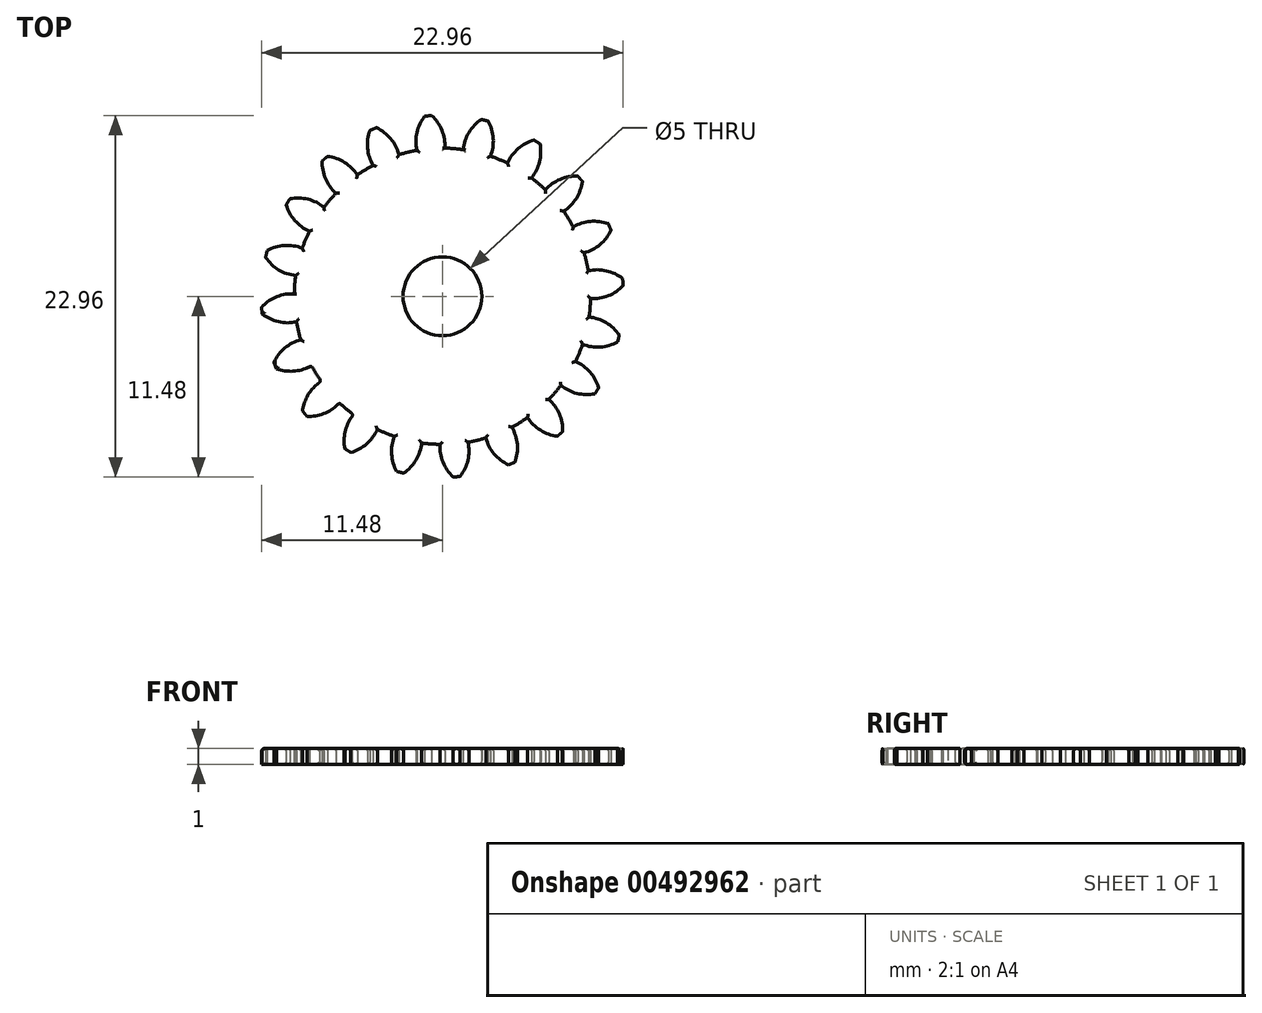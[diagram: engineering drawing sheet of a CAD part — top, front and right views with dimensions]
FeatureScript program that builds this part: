
annotation { "Feature Type Name" : "Feature", "Feature Type Description" : "" }
export const myFeature = defineFeature(function(context is Context, id is Id, definition is map)
    precondition{}
    {
        {
            assignVariable(context, id + "F0", {"name" : "GearDepth", "anyValue" : 1});
        }
        {
            var Q0;
            Q0=qCreatedBy(makeId("Top.planeOp"),FACE);
            var sketch = newSketch(context, id + "F1", { "sketchPlane" : qUnion([Q0])});
            skCircle(sketch, "E0", {"center": v(0, 0) * mm, "radius": 9.4 * mm});
            skCircle(sketch, "E1", {"center": v(0, 0) * mm, "radius": 10.45 * mm, "construction": true});
            skCircle(sketch, "E2", {"center": v(0, 0) * mm, "radius": 11.5 * mm, "construction": true});
            skLineSegment(sketch, "E3", {"start": v(0, 0) * mm, "end": v(0, 17.6) * mm, "construction": true});
            skLineSegment(sketch, "E4", {"start": v(0, 0) * mm, "end": v(-1.42, 18) * mm, "construction": true});
            skLineSegment(sketch, "E5", {"start": v(0, 10.45) * mm, "end": v(-10.54, 10.45) * mm, "construction": true});
            skLineSegment(sketch, "E6", {"start": v(0, 10.45) * mm, "end": v(-10.3, 6.7) * mm, "construction": true});
            skCircle(sketch, "E7", {"center": v(0, 10.45) * mm, "radius": 2.61 * mm, "construction": true});
            skCircle(sketch, "E8", {"center": v(-2.46, 9.56) * mm, "radius": 2.61 * mm, "construction": true});
            skArc(sketch, "E9", {"start": v(-4.91, 10.45) * mm, "mid": v(-4.92, 10.42) * mm, "end": v(-4.94, 10.39) * mm});
            skArc(sketch, "E10.trimOffspring", {"start": v(0.15, 9.4) * mm, "mid": v(-0.03, 10.54) * mm, "end": v(-0.68, 11.48) * mm});
            skArc(sketch, "E11.MirrorCS", {"start": v(-1.62, 9.27) * mm, "mid": v(-1.62, 10.41) * mm, "end": v(-1.12, 11.45) * mm});
            skLineSegment(sketch, "E12", {"start": v(-1.12, 11.45) * mm, "end": v(-0.68, 11.48) * mm});
            skArc(sketch, "E13.1.0", {"start": v(-2.76, 9) * mm, "mid": v(-3.29, 10.01) * mm, "end": v(-4.2, 10.7) * mm});
            skLineSegment(sketch, "E13.1.1", {"start": v(-4.6, 10.54) * mm, "end": v(-4.2, 10.7) * mm});
            skArc(sketch, "E13.1.2", {"start": v(-4.4, 8.31) * mm, "mid": v(-4.76, 9.4) * mm, "end": v(-4.6, 10.54) * mm});
            skArc(sketch, "E13.2.0", {"start": v(-5.4, 7.7) * mm, "mid": v(-6.22, 8.5) * mm, "end": v(-7.3, 8.89) * mm});
            skLineSegment(sketch, "E13.2.1", {"start": v(-7.64, 8.6) * mm, "end": v(-7.3, 8.89) * mm});
            skArc(sketch, "E13.2.2", {"start": v(-6.76, 6.54) * mm, "mid": v(-7.43, 7.47) * mm, "end": v(-7.64, 8.6) * mm});
            skArc(sketch, "E13.3.0", {"start": v(-7.52, 5.65) * mm, "mid": v(-8.54, 6.17) * mm, "end": v(-9.69, 6.2) * mm});
            skLineSegment(sketch, "E13.3.1", {"start": v(-9.92, 5.82) * mm, "end": v(-9.69, 6.2) * mm});
            skArc(sketch, "E13.3.2", {"start": v(-8.45, 4.13) * mm, "mid": v(-9.37, 4.81) * mm, "end": v(-9.92, 5.82) * mm});
            skArc(sketch, "E13.4.0", {"start": v(-8.9, 3.05) * mm, "mid": v(-10.03, 3.23) * mm, "end": v(-11.13, 2.9) * mm});
            skLineSegment(sketch, "E13.4.1", {"start": v(-11.23, 2.47) * mm, "end": v(-11.13, 2.9) * mm});
            skArc(sketch, "E13.4.2", {"start": v(-9.32, 1.32) * mm, "mid": v(-10.4, 1.68) * mm, "end": v(-11.23, 2.47) * mm});
            skArc(sketch, "E13.5.0", {"start": v(-9.4, 0.15) * mm, "mid": v(-10.54, -0.03) * mm, "end": v(-11.48, -0.68) * mm});
            skLineSegment(sketch, "E13.5.1", {"start": v(-11.45, -1.12) * mm, "end": v(-11.48, -0.68) * mm});
            skArc(sketch, "E13.5.2", {"start": v(-9.27, -1.62) * mm, "mid": v(-10.41, -1.62) * mm, "end": v(-11.45, -1.12) * mm});
            skArc(sketch, "E13.6.0", {"start": v(-9, -2.76) * mm, "mid": v(-10.01, -3.29) * mm, "end": v(-10.7, -4.2) * mm});
            skLineSegment(sketch, "E13.6.1", {"start": v(-10.54, -4.6) * mm, "end": v(-10.7, -4.2) * mm});
            skArc(sketch, "E13.6.2", {"start": v(-8.31, -4.4) * mm, "mid": v(-9.4, -4.76) * mm, "end": v(-10.54, -4.6) * mm});
            skArc(sketch, "E13.7.0", {"start": v(-7.7, -5.4) * mm, "mid": v(-8.5, -6.22) * mm, "end": v(-8.89, -7.3) * mm});
            skLineSegment(sketch, "E13.7.1", {"start": v(-8.6, -7.64) * mm, "end": v(-8.89, -7.3) * mm});
            skArc(sketch, "E13.7.2", {"start": v(-6.54, -6.76) * mm, "mid": v(-7.47, -7.43) * mm, "end": v(-8.6, -7.64) * mm});
            skArc(sketch, "E13.8.0", {"start": v(-5.65, -7.52) * mm, "mid": v(-6.17, -8.54) * mm, "end": v(-6.2, -9.69) * mm});
            skLineSegment(sketch, "E13.8.1", {"start": v(-5.82, -9.92) * mm, "end": v(-6.2, -9.69) * mm});
            skArc(sketch, "E13.8.2", {"start": v(-4.13, -8.45) * mm, "mid": v(-4.81, -9.37) * mm, "end": v(-5.82, -9.92) * mm});
            skArc(sketch, "E13.9.0", {"start": v(-3.05, -8.9) * mm, "mid": v(-3.23, -10.03) * mm, "end": v(-2.9, -11.13) * mm});
            skLineSegment(sketch, "E13.9.1", {"start": v(-2.47, -11.23) * mm, "end": v(-2.9, -11.13) * mm});
            skArc(sketch, "E13.9.2", {"start": v(-1.32, -9.32) * mm, "mid": v(-1.68, -10.4) * mm, "end": v(-2.47, -11.23) * mm});
            skArc(sketch, "E13.10.0", {"start": v(-0.15, -9.4) * mm, "mid": v(0.03, -10.54) * mm, "end": v(0.68, -11.48) * mm});
            skLineSegment(sketch, "E13.10.1", {"start": v(1.12, -11.45) * mm, "end": v(0.68, -11.48) * mm});
            skArc(sketch, "E13.10.2", {"start": v(1.62, -9.27) * mm, "mid": v(1.62, -10.41) * mm, "end": v(1.12, -11.45) * mm});
            skArc(sketch, "E13.11.0", {"start": v(2.76, -9) * mm, "mid": v(3.29, -10.01) * mm, "end": v(4.2, -10.7) * mm});
            skLineSegment(sketch, "E13.11.1", {"start": v(4.6, -10.54) * mm, "end": v(4.2, -10.7) * mm});
            skArc(sketch, "E13.11.2", {"start": v(4.4, -8.31) * mm, "mid": v(4.76, -9.4) * mm, "end": v(4.6, -10.54) * mm});
            skArc(sketch, "E13.12.0", {"start": v(5.4, -7.7) * mm, "mid": v(6.22, -8.5) * mm, "end": v(7.3, -8.89) * mm});
            skLineSegment(sketch, "E13.12.1", {"start": v(7.64, -8.6) * mm, "end": v(7.3, -8.89) * mm});
            skArc(sketch, "E13.12.2", {"start": v(6.76, -6.54) * mm, "mid": v(7.43, -7.47) * mm, "end": v(7.64, -8.6) * mm});
            skArc(sketch, "E13.13.0", {"start": v(7.52, -5.65) * mm, "mid": v(8.54, -6.17) * mm, "end": v(9.69, -6.2) * mm});
            skLineSegment(sketch, "E13.13.1", {"start": v(9.92, -5.82) * mm, "end": v(9.69, -6.2) * mm});
            skArc(sketch, "E13.13.2", {"start": v(8.45, -4.13) * mm, "mid": v(9.37, -4.81) * mm, "end": v(9.92, -5.82) * mm});
            skArc(sketch, "E13.14.0", {"start": v(8.9, -3.05) * mm, "mid": v(10.03, -3.23) * mm, "end": v(11.13, -2.9) * mm});
            skLineSegment(sketch, "E13.14.1", {"start": v(11.23, -2.47) * mm, "end": v(11.13, -2.9) * mm});
            skArc(sketch, "E13.14.2", {"start": v(9.32, -1.32) * mm, "mid": v(10.4, -1.68) * mm, "end": v(11.23, -2.47) * mm});
            skArc(sketch, "E13.15.0", {"start": v(9.4, -0.15) * mm, "mid": v(10.54, 0.03) * mm, "end": v(11.48, 0.68) * mm});
            skLineSegment(sketch, "E13.15.1", {"start": v(11.45, 1.12) * mm, "end": v(11.48, 0.68) * mm});
            skArc(sketch, "E13.15.2", {"start": v(9.27, 1.62) * mm, "mid": v(10.41, 1.62) * mm, "end": v(11.45, 1.12) * mm});
            skArc(sketch, "E13.16.0", {"start": v(9, 2.76) * mm, "mid": v(10.01, 3.29) * mm, "end": v(10.7, 4.2) * mm});
            skLineSegment(sketch, "E13.16.1", {"start": v(10.54, 4.6) * mm, "end": v(10.7, 4.2) * mm});
            skArc(sketch, "E13.16.2", {"start": v(8.31, 4.4) * mm, "mid": v(9.4, 4.76) * mm, "end": v(10.54, 4.6) * mm});
            skArc(sketch, "E13.17.0", {"start": v(7.7, 5.4) * mm, "mid": v(8.5, 6.22) * mm, "end": v(8.89, 7.3) * mm});
            skLineSegment(sketch, "E13.17.1", {"start": v(8.6, 7.64) * mm, "end": v(8.89, 7.3) * mm});
            skArc(sketch, "E13.17.2", {"start": v(6.54, 6.76) * mm, "mid": v(7.47, 7.43) * mm, "end": v(8.6, 7.64) * mm});
            skArc(sketch, "E13.18.0", {"start": v(5.65, 7.52) * mm, "mid": v(6.17, 8.54) * mm, "end": v(6.2, 9.69) * mm});
            skLineSegment(sketch, "E13.18.1", {"start": v(5.82, 9.92) * mm, "end": v(6.2, 9.69) * mm});
            skArc(sketch, "E13.18.2", {"start": v(4.13, 8.45) * mm, "mid": v(4.81, 9.37) * mm, "end": v(5.82, 9.92) * mm});
            skArc(sketch, "E13.19.0", {"start": v(3.05, 8.9) * mm, "mid": v(3.23, 10.03) * mm, "end": v(2.9, 11.13) * mm});
            skLineSegment(sketch, "E13.19.1", {"start": v(2.47, 11.23) * mm, "end": v(2.9, 11.13) * mm});
            skArc(sketch, "E13.19.2", {"start": v(1.32, 9.32) * mm, "mid": v(1.68, 10.4) * mm, "end": v(2.47, 11.23) * mm});
            skCircle(sketch, "E14", {"center": v(0, 0) * mm, "radius": 2.5 * mm});
            skSolve(sketch);
        }
        {
            var Q0;
            {var subQ0=sQuery(id+"F1.wireOp",EDGE,"E10.trimOffspring");Q0=makeQuery(id+"F1.imprint","IMPRINT",FACE,{"disambiguationData":[TD([[makeQuery(id+"F1.imprint","IMPRINT",EDGE,{"derivedFrom":subQ0}),1.0]])]});}
            var Q1;
            {var subQ0=sQuery(id+"F1.wireOp",EDGE,"E0");var subQ1=makeQuery(id+"F1.imprint","INTERSECT",VERTEX,{"derivedFrom":[subQ0,sQuery(id+"F1.wireOp",EDGE,"E10.trimOffspring")]});Q1=makeQuery(id+"F1.imprint","IMPRINT",FACE,{"disambiguationData":[TD([[makeQuery(id+"F1.imprint","IMPRINT",EDGE,{"disambiguationData":[TD([[subQ1,-1.0]])],"derivedFrom":subQ0}),1.0]])]});}
            var Q2;
            {var subQ0=sQuery(id+"F1.wireOp",EDGE,"E13.1.0");Q2=makeQuery(id+"F1.imprint","IMPRINT",FACE,{"disambiguationData":[TD([[makeQuery(id+"F1.imprint","IMPRINT",EDGE,{"derivedFrom":subQ0}),1.0]])]});}
            var Q3;
            {var subQ0=sQuery(id+"F1.wireOp",EDGE,"E13.2.0");Q3=makeQuery(id+"F1.imprint","IMPRINT",FACE,{"disambiguationData":[TD([[makeQuery(id+"F1.imprint","IMPRINT",EDGE,{"derivedFrom":subQ0}),1.0]])]});}
            var Q4;
            {var subQ0=sQuery(id+"F1.wireOp",EDGE,"E13.3.0");Q4=makeQuery(id+"F1.imprint","IMPRINT",FACE,{"disambiguationData":[TD([[makeQuery(id+"F1.imprint","IMPRINT",EDGE,{"derivedFrom":subQ0}),1.0]])]});}
            var Q5;
            {var subQ0=sQuery(id+"F1.wireOp",EDGE,"E13.4.0");Q5=makeQuery(id+"F1.imprint","IMPRINT",FACE,{"disambiguationData":[TD([[makeQuery(id+"F1.imprint","IMPRINT",EDGE,{"derivedFrom":subQ0}),1.0]])]});}
            var Q6;
            {var subQ0=sQuery(id+"F1.wireOp",EDGE,"E13.5.0");Q6=makeQuery(id+"F1.imprint","IMPRINT",FACE,{"disambiguationData":[TD([[makeQuery(id+"F1.imprint","IMPRINT",EDGE,{"derivedFrom":subQ0}),1.0]])]});}
            var Q7;
            {var subQ0=sQuery(id+"F1.wireOp",EDGE,"E13.6.0");Q7=makeQuery(id+"F1.imprint","IMPRINT",FACE,{"disambiguationData":[TD([[makeQuery(id+"F1.imprint","IMPRINT",EDGE,{"derivedFrom":subQ0}),1.0]])]});}
            var Q8;
            {var subQ0=sQuery(id+"F1.wireOp",EDGE,"E13.7.0");Q8=makeQuery(id+"F1.imprint","IMPRINT",FACE,{"disambiguationData":[TD([[makeQuery(id+"F1.imprint","IMPRINT",EDGE,{"derivedFrom":subQ0}),1.0]])]});}
            var Q9;
            {var subQ0=sQuery(id+"F1.wireOp",EDGE,"E13.8.0");Q9=makeQuery(id+"F1.imprint","IMPRINT",FACE,{"disambiguationData":[TD([[makeQuery(id+"F1.imprint","IMPRINT",EDGE,{"derivedFrom":subQ0}),1.0]])]});}
            var Q10;
            {var subQ0=sQuery(id+"F1.wireOp",EDGE,"E13.9.0");Q10=makeQuery(id+"F1.imprint","IMPRINT",FACE,{"disambiguationData":[TD([[makeQuery(id+"F1.imprint","IMPRINT",EDGE,{"derivedFrom":subQ0}),1.0]])]});}
            var Q11;
            {var subQ0=sQuery(id+"F1.wireOp",EDGE,"E13.10.0");Q11=makeQuery(id+"F1.imprint","IMPRINT",FACE,{"disambiguationData":[TD([[makeQuery(id+"F1.imprint","IMPRINT",EDGE,{"derivedFrom":subQ0}),1.0]])]});}
            var Q12;
            {var subQ0=sQuery(id+"F1.wireOp",EDGE,"E13.11.0");Q12=makeQuery(id+"F1.imprint","IMPRINT",FACE,{"disambiguationData":[TD([[makeQuery(id+"F1.imprint","IMPRINT",EDGE,{"derivedFrom":subQ0}),1.0]])]});}
            var Q13;
            {var subQ0=sQuery(id+"F1.wireOp",EDGE,"E13.12.0");Q13=makeQuery(id+"F1.imprint","IMPRINT",FACE,{"disambiguationData":[TD([[makeQuery(id+"F1.imprint","IMPRINT",EDGE,{"derivedFrom":subQ0}),1.0]])]});}
            var Q14;
            {var subQ0=sQuery(id+"F1.wireOp",EDGE,"E13.13.0");Q14=makeQuery(id+"F1.imprint","IMPRINT",FACE,{"disambiguationData":[TD([[makeQuery(id+"F1.imprint","IMPRINT",EDGE,{"derivedFrom":subQ0}),1.0]])]});}
            var Q15;
            {var subQ0=sQuery(id+"F1.wireOp",EDGE,"E13.14.0");Q15=makeQuery(id+"F1.imprint","IMPRINT",FACE,{"disambiguationData":[TD([[makeQuery(id+"F1.imprint","IMPRINT",EDGE,{"derivedFrom":subQ0}),1.0]])]});}
            var Q16;
            {var subQ0=sQuery(id+"F1.wireOp",EDGE,"E13.15.0");Q16=makeQuery(id+"F1.imprint","IMPRINT",FACE,{"disambiguationData":[TD([[makeQuery(id+"F1.imprint","IMPRINT",EDGE,{"derivedFrom":subQ0}),1.0]])]});}
            var Q17;
            {var subQ0=sQuery(id+"F1.wireOp",EDGE,"E13.16.0");Q17=makeQuery(id+"F1.imprint","IMPRINT",FACE,{"disambiguationData":[TD([[makeQuery(id+"F1.imprint","IMPRINT",EDGE,{"derivedFrom":subQ0}),1.0]])]});}
            var Q18;
            {var subQ0=sQuery(id+"F1.wireOp",EDGE,"E13.17.0");Q18=makeQuery(id+"F1.imprint","IMPRINT",FACE,{"disambiguationData":[TD([[makeQuery(id+"F1.imprint","IMPRINT",EDGE,{"derivedFrom":subQ0}),1.0]])]});}
            var Q19;
            {var subQ0=sQuery(id+"F1.wireOp",EDGE,"E13.18.0");Q19=makeQuery(id+"F1.imprint","IMPRINT",FACE,{"disambiguationData":[TD([[makeQuery(id+"F1.imprint","IMPRINT",EDGE,{"derivedFrom":subQ0}),1.0]])]});}
            var Q20;
            {var subQ0=sQuery(id+"F1.wireOp",EDGE,"E13.19.0");Q20=makeQuery(id+"F1.imprint","IMPRINT",FACE,{"disambiguationData":[TD([[makeQuery(id+"F1.imprint","IMPRINT",EDGE,{"derivedFrom":subQ0}),1.0]])]});}
            var Q21;
            Q21=sQuery(id+"F1.wireOp",EDGE,"E0");
            var Q22;
            Q22=sQuery(id+"F1.wireOp",EDGE,"E10.trimOffspring");
            var Q23;
            Q23=sQuery(id+"F1.wireOp",EDGE,"E12");
            var Q24;
            Q24=sQuery(id+"F1.wireOp",EDGE,"E11.MirrorCS");
            extrude(context, id + "F2", {"entities" : qUnion([Q0, Q1, Q2, Q3, Q4, Q5, Q6, Q7, Q8, Q9, Q10, Q11, Q12, Q13, Q14, Q15, Q16, Q17, Q18, Q19, Q20]), "surfaceEntities" : qUnion([Q21, Q22, Q23, Q24]), "depth" : (getVariable(context, 'GearDepth')) * mm});
        }
        {
            var Q0;
            Q0=makeQuery(id+"F2.opExtrude","CAP_EDGE",EDGE,{"disambiguationData":[OSD([sQuery(id+"F1.wireOp",EDGE,"E13.5.2")])],"isStart":false});
            var Q1;
            Q1=makeQuery(id+"F2.opExtrude","CAP_EDGE",EDGE,{"disambiguationData":[OSD([sQuery(id+"F1.wireOp",EDGE,"E13.5.1")])],"isStart":false});
            var Q2;
            {var subQ0=sQuery(id+"F1.wireOp",EDGE,"E0");Q2=makeQuery(id+"F2.opExtrude","CAP_EDGE",EDGE,{"disambiguationData":[OSD([subQ0]),TDD([makeQuery(id+"F1.imprint","IMPRINT",EDGE,{"disambiguationData":[TD([[makeQuery(id+"F1.imprint","INTERSECT",VERTEX,{"derivedFrom":[subQ0,sQuery(id+"F1.wireOp",EDGE,"E13.5.2")]}),-1.0]])],"derivedFrom":subQ0})])],"isStart":false});}
            var Q3;
            Q3=makeQuery(id+"F2.opExtrude","CAP_EDGE",EDGE,{"disambiguationData":[OSD([sQuery(id+"F1.wireOp",EDGE,"E13.6.0")])],"isStart":false});
            var Q4;
            Q4=makeQuery(id+"F2.opExtrude","CAP_EDGE",EDGE,{"disambiguationData":[OSD([sQuery(id+"F1.wireOp",EDGE,"E13.6.1")])],"isStart":false});
            var Q5;
            Q5=makeQuery(id+"F2.opExtrude","CAP_EDGE",EDGE,{"disambiguationData":[OSD([sQuery(id+"F1.wireOp",EDGE,"E13.6.2")])],"isStart":false});
            var Q6;
            {var subQ0=sQuery(id+"F1.wireOp",EDGE,"E0");Q6=makeQuery(id+"F2.opExtrude","SWEPT_FACE",FACE,{"disambiguationData":[OSD([subQ0]),TDD([makeQuery(id+"F1.imprint","IMPRINT",EDGE,{"disambiguationData":[TD([[makeQuery(id+"F1.imprint","INTERSECT",VERTEX,{"derivedFrom":[subQ0,sQuery(id+"F1.wireOp",EDGE,"E13.6.2")]}),-1.0]])],"derivedFrom":subQ0})])]});}
            var Q7;
            {var subQ0=sQuery(id+"F1.wireOp",EDGE,"E0");Q7=makeQuery(id+"F2.opExtrude","CAP_EDGE",EDGE,{"disambiguationData":[OSD([subQ0]),TDD([makeQuery(id+"F1.imprint","IMPRINT",EDGE,{"disambiguationData":[TD([[makeQuery(id+"F1.imprint","INTERSECT",VERTEX,{"derivedFrom":[subQ0,sQuery(id+"F1.wireOp",EDGE,"E13.6.2")]}),-1.0]])],"derivedFrom":subQ0})])],"isStart":false});}
            var Q8;
            Q8=makeQuery(id+"F2.opExtrude","CAP_EDGE",EDGE,{"disambiguationData":[OSD([sQuery(id+"F1.wireOp",EDGE,"E13.7.2")])],"isStart":true});
            var Q9;
            {var subQ0=sQuery(id+"F1.wireOp",EDGE,"E0");Q9=makeQuery(id+"F2.opExtrude","CAP_EDGE",EDGE,{"disambiguationData":[OSD([subQ0]),TDD([makeQuery(id+"F1.imprint","IMPRINT",EDGE,{"disambiguationData":[TD([[makeQuery(id+"F1.imprint","INTERSECT",VERTEX,{"derivedFrom":[subQ0,sQuery(id+"F1.wireOp",EDGE,"E13.7.2")]}),-1.0]])],"derivedFrom":subQ0})])],"isStart":true});}
            var Q10;
            Q10=makeQuery(id+"F2.opExtrude","CAP_EDGE",EDGE,{"disambiguationData":[OSD([sQuery(id+"F1.wireOp",EDGE,"E13.7.2")])],"isStart":false});
            var Q11;
            {var subQ0=sQuery(id+"F1.wireOp",EDGE,"E0");Q11=makeQuery(id+"F2.opExtrude","CAP_EDGE",EDGE,{"disambiguationData":[OSD([subQ0]),TDD([makeQuery(id+"F1.imprint","IMPRINT",EDGE,{"disambiguationData":[TD([[makeQuery(id+"F1.imprint","INTERSECT",VERTEX,{"derivedFrom":[subQ0,sQuery(id+"F1.wireOp",EDGE,"E13.7.2")]}),-1.0]])],"derivedFrom":subQ0})])],"isStart":false});}
            var Q12;
            Q12=makeQuery(id+"F2.opExtrude","CAP_EDGE",EDGE,{"disambiguationData":[OSD([sQuery(id+"F1.wireOp",EDGE,"E13.8.0")])],"isStart":false});
            var Q13;
            {var subQ0=sQuery(id+"F1.wireOp",EDGE,"E0");Q13=makeQuery(id+"F2.opExtrude","SWEPT_FACE",FACE,{"disambiguationData":[OSD([subQ0]),TDD([makeQuery(id+"F1.imprint","IMPRINT",EDGE,{"disambiguationData":[TD([[makeQuery(id+"F1.imprint","INTERSECT",VERTEX,{"derivedFrom":[subQ0,sQuery(id+"F1.wireOp",EDGE,"E13.7.2")]}),-1.0]])],"derivedFrom":subQ0})])]});}
            var Q14;
            Q14=makeQuery(id+"F2.opExtrude","CAP_EDGE",EDGE,{"disambiguationData":[OSD([sQuery(id+"F1.wireOp",EDGE,"E13.6.0")])],"isStart":true});
            var Q15;
            Q15=makeQuery(id+"F2.opExtrude","CAP_EDGE",EDGE,{"disambiguationData":[OSD([sQuery(id+"F1.wireOp",EDGE,"E13.8.2")])],"isStart":false});
            var Q16;
            {var subQ0=sQuery(id+"F1.wireOp",EDGE,"E0");Q16=makeQuery(id+"F2.opExtrude","CAP_EDGE",EDGE,{"disambiguationData":[OSD([subQ0]),TDD([makeQuery(id+"F1.imprint","IMPRINT",EDGE,{"disambiguationData":[TD([[makeQuery(id+"F1.imprint","INTERSECT",VERTEX,{"derivedFrom":[subQ0,sQuery(id+"F1.wireOp",EDGE,"E13.8.2")]}),-1.0]])],"derivedFrom":subQ0})])],"isStart":false});}
            var Q17;
            Q17=makeQuery(id+"F2.opExtrude","CAP_EDGE",EDGE,{"disambiguationData":[OSD([sQuery(id+"F1.wireOp",EDGE,"E13.9.0")])],"isStart":false});
            var Q18;
            Q18=makeQuery(id+"F2.opExtrude","CAP_EDGE",EDGE,{"disambiguationData":[OSD([sQuery(id+"F1.wireOp",EDGE,"E13.9.2")])],"isStart":false});
            var Q19;
            {var subQ0=sQuery(id+"F1.wireOp",EDGE,"E0");Q19=makeQuery(id+"F2.opExtrude","CAP_EDGE",EDGE,{"disambiguationData":[OSD([subQ0]),TDD([makeQuery(id+"F1.imprint","IMPRINT",EDGE,{"disambiguationData":[TD([[makeQuery(id+"F1.imprint","INTERSECT",VERTEX,{"derivedFrom":[subQ0,sQuery(id+"F1.wireOp",EDGE,"E13.9.2")]}),-1.0]])],"derivedFrom":subQ0})])],"isStart":false});}
            var Q20;
            Q20=makeQuery(id+"F2.opExtrude","CAP_EDGE",EDGE,{"disambiguationData":[OSD([sQuery(id+"F1.wireOp",EDGE,"E13.10.0")])],"isStart":false});
            var Q21;
            Q21=makeQuery(id+"F2.opExtrude","CAP_EDGE",EDGE,{"disambiguationData":[OSD([sQuery(id+"F1.wireOp",EDGE,"E13.10.2")])],"isStart":false});
            var Q22;
            {var subQ0=sQuery(id+"F1.wireOp",EDGE,"E0");Q22=makeQuery(id+"F2.opExtrude","CAP_EDGE",EDGE,{"disambiguationData":[OSD([subQ0]),TDD([makeQuery(id+"F1.imprint","IMPRINT",EDGE,{"disambiguationData":[TD([[makeQuery(id+"F1.imprint","INTERSECT",VERTEX,{"derivedFrom":[subQ0,sQuery(id+"F1.wireOp",EDGE,"E13.10.2")]}),-1.0]])],"derivedFrom":subQ0})])],"isStart":false});}
            var Q23;
            Q23=makeQuery(id+"F2.opExtrude","CAP_EDGE",EDGE,{"disambiguationData":[OSD([sQuery(id+"F1.wireOp",EDGE,"E13.11.0")])],"isStart":false});
            var Q24;
            Q24=makeQuery(id+"F2.opExtrude","CAP_EDGE",EDGE,{"disambiguationData":[OSD([sQuery(id+"F1.wireOp",EDGE,"E13.11.2")])],"isStart":false});
            var Q25;
            {var subQ0=sQuery(id+"F1.wireOp",EDGE,"E0");Q25=makeQuery(id+"F2.opExtrude","CAP_EDGE",EDGE,{"disambiguationData":[OSD([subQ0]),TDD([makeQuery(id+"F1.imprint","IMPRINT",EDGE,{"disambiguationData":[TD([[makeQuery(id+"F1.imprint","INTERSECT",VERTEX,{"derivedFrom":[subQ0,sQuery(id+"F1.wireOp",EDGE,"E13.11.2")]}),-1.0]])],"derivedFrom":subQ0})])],"isStart":false});}
            var Q26;
            Q26=makeQuery(id+"F2.opExtrude","CAP_EDGE",EDGE,{"disambiguationData":[OSD([sQuery(id+"F1.wireOp",EDGE,"E13.12.0")])],"isStart":false});
            var Q27;
            Q27=makeQuery(id+"F2.opExtrude","CAP_EDGE",EDGE,{"disambiguationData":[OSD([sQuery(id+"F1.wireOp",EDGE,"E13.12.2")])],"isStart":false});
            var Q28;
            {var subQ0=sQuery(id+"F1.wireOp",EDGE,"E0");Q28=makeQuery(id+"F2.opExtrude","CAP_EDGE",EDGE,{"disambiguationData":[OSD([subQ0]),TDD([makeQuery(id+"F1.imprint","IMPRINT",EDGE,{"disambiguationData":[TD([[makeQuery(id+"F1.imprint","INTERSECT",VERTEX,{"derivedFrom":[subQ0,sQuery(id+"F1.wireOp",EDGE,"E13.12.2")]}),-1.0]])],"derivedFrom":subQ0})])],"isStart":false});}
            var Q29;
            Q29=makeQuery(id+"F2.opExtrude","CAP_EDGE",EDGE,{"disambiguationData":[OSD([sQuery(id+"F1.wireOp",EDGE,"E13.13.0")])],"isStart":false});
            var Q30;
            Q30=makeQuery(id+"F2.opExtrude","CAP_EDGE",EDGE,{"disambiguationData":[OSD([sQuery(id+"F1.wireOp",EDGE,"E13.13.2")])],"isStart":false});
            var Q31;
            {var subQ0=sQuery(id+"F1.wireOp",EDGE,"E0");Q31=makeQuery(id+"F2.opExtrude","CAP_EDGE",EDGE,{"disambiguationData":[OSD([subQ0]),TDD([makeQuery(id+"F1.imprint","IMPRINT",EDGE,{"disambiguationData":[TD([[makeQuery(id+"F1.imprint","INTERSECT",VERTEX,{"derivedFrom":[subQ0,sQuery(id+"F1.wireOp",EDGE,"E13.13.2")]}),-1.0]])],"derivedFrom":subQ0})])],"isStart":false});}
            var Q32;
            Q32=makeQuery(id+"F2.opExtrude","CAP_EDGE",EDGE,{"disambiguationData":[OSD([sQuery(id+"F1.wireOp",EDGE,"E13.14.0")])],"isStart":false});
            var Q33;
            Q33=makeQuery(id+"F2.opExtrude","CAP_EDGE",EDGE,{"disambiguationData":[OSD([sQuery(id+"F1.wireOp",EDGE,"E13.14.2")])],"isStart":false});
            var Q34;
            {var subQ0=sQuery(id+"F1.wireOp",EDGE,"E0");Q34=makeQuery(id+"F2.opExtrude","CAP_EDGE",EDGE,{"disambiguationData":[OSD([subQ0]),TDD([makeQuery(id+"F1.imprint","IMPRINT",EDGE,{"disambiguationData":[TD([[makeQuery(id+"F1.imprint","INTERSECT",VERTEX,{"derivedFrom":[subQ0,sQuery(id+"F1.wireOp",EDGE,"E13.14.2")]}),-1.0]])],"derivedFrom":subQ0})])],"isStart":false});}
            var Q35;
            Q35=makeQuery(id+"F2.opExtrude","CAP_EDGE",EDGE,{"disambiguationData":[OSD([sQuery(id+"F1.wireOp",EDGE,"E13.15.0")])],"isStart":false});
            var Q36;
            {var subQ0=sQuery(id+"F1.wireOp",EDGE,"E0");Q36=makeQuery(id+"F2.opExtrude","CAP_EDGE",EDGE,{"disambiguationData":[OSD([subQ0]),TDD([makeQuery(id+"F1.imprint","IMPRINT",EDGE,{"disambiguationData":[TD([[makeQuery(id+"F1.imprint","INTERSECT",VERTEX,{"derivedFrom":[subQ0,sQuery(id+"F1.wireOp",EDGE,"E13.14.2")]}),-1.0]])],"derivedFrom":subQ0})])],"isStart":false});}
            var Q37;
            Q37=makeQuery(id+"F2.opExtrude","CAP_EDGE",EDGE,{"disambiguationData":[OSD([sQuery(id+"F1.wireOp",EDGE,"E13.15.2")])],"isStart":false});
            var Q38;
            {var subQ0=sQuery(id+"F1.wireOp",EDGE,"E0");Q38=makeQuery(id+"F2.opExtrude","CAP_EDGE",EDGE,{"disambiguationData":[OSD([subQ0]),TDD([makeQuery(id+"F1.imprint","IMPRINT",EDGE,{"disambiguationData":[TD([[makeQuery(id+"F1.imprint","INTERSECT",VERTEX,{"derivedFrom":[subQ0,sQuery(id+"F1.wireOp",EDGE,"E13.15.2")]}),-1.0]])],"derivedFrom":subQ0})])],"isStart":false});}
            var Q39;
            Q39=makeQuery(id+"F2.opExtrude","CAP_EDGE",EDGE,{"disambiguationData":[OSD([sQuery(id+"F1.wireOp",EDGE,"E13.16.0")])],"isStart":false});
            var Q40;
            Q40=makeQuery(id+"F2.opExtrude","CAP_EDGE",EDGE,{"disambiguationData":[OSD([sQuery(id+"F1.wireOp",EDGE,"E13.16.2")])],"isStart":false});
            var Q41;
            Q41=makeQuery(id+"F2.opExtrude","CAP_EDGE",EDGE,{"disambiguationData":[OSD([sQuery(id+"F1.wireOp",EDGE,"E13.17.0")])],"isStart":false});
            var Q42;
            {var subQ0=sQuery(id+"F1.wireOp",EDGE,"E0");Q42=makeQuery(id+"F2.opExtrude","CAP_EDGE",EDGE,{"disambiguationData":[OSD([subQ0]),TDD([makeQuery(id+"F1.imprint","IMPRINT",EDGE,{"disambiguationData":[TD([[makeQuery(id+"F1.imprint","INTERSECT",VERTEX,{"derivedFrom":[subQ0,sQuery(id+"F1.wireOp",EDGE,"E13.16.2")]}),-1.0]])],"derivedFrom":subQ0})])],"isStart":false});}
            var Q43;
            Q43=makeQuery(id+"F2.opExtrude","CAP_EDGE",EDGE,{"disambiguationData":[OSD([sQuery(id+"F1.wireOp",EDGE,"E13.17.2")])],"isStart":false});
            var Q44;
            {var subQ0=sQuery(id+"F1.wireOp",EDGE,"E0");Q44=makeQuery(id+"F2.opExtrude","CAP_EDGE",EDGE,{"disambiguationData":[OSD([subQ0]),TDD([makeQuery(id+"F1.imprint","IMPRINT",EDGE,{"disambiguationData":[TD([[makeQuery(id+"F1.imprint","INTERSECT",VERTEX,{"derivedFrom":[subQ0,sQuery(id+"F1.wireOp",EDGE,"E13.17.2")]}),-1.0]])],"derivedFrom":subQ0})])],"isStart":false});}
            var Q45;
            Q45=makeQuery(id+"F2.opExtrude","CAP_EDGE",EDGE,{"disambiguationData":[OSD([sQuery(id+"F1.wireOp",EDGE,"E13.18.0")])],"isStart":false});
            var Q46;
            Q46=makeQuery(id+"F2.opExtrude","CAP_EDGE",EDGE,{"disambiguationData":[OSD([sQuery(id+"F1.wireOp",EDGE,"E13.18.2")])],"isStart":false});
            var Q47;
            {var subQ0=sQuery(id+"F1.wireOp",EDGE,"E0");Q47=makeQuery(id+"F2.opExtrude","CAP_EDGE",EDGE,{"disambiguationData":[OSD([subQ0]),TDD([makeQuery(id+"F1.imprint","IMPRINT",EDGE,{"disambiguationData":[TD([[makeQuery(id+"F1.imprint","INTERSECT",VERTEX,{"derivedFrom":[subQ0,sQuery(id+"F1.wireOp",EDGE,"E13.18.2")]}),-1.0]])],"derivedFrom":subQ0})])],"isStart":false});}
            var Q48;
            Q48=makeQuery(id+"F2.opExtrude","CAP_EDGE",EDGE,{"disambiguationData":[OSD([sQuery(id+"F1.wireOp",EDGE,"E13.19.0")])],"isStart":false});
            var Q49;
            Q49=makeQuery(id+"F2.opExtrude","CAP_EDGE",EDGE,{"disambiguationData":[OSD([sQuery(id+"F1.wireOp",EDGE,"E13.19.2")])],"isStart":false});
            var Q50;
            Q50=makeQuery(id+"F2.opExtrude","CAP_EDGE",EDGE,{"disambiguationData":[OSD([sQuery(id+"F1.wireOp",EDGE,"E10.trimOffspring")])],"isStart":false});
            var Q51;
            Q51=makeQuery(id+"F2.opExtrude","CAP_EDGE",EDGE,{"disambiguationData":[OSD([sQuery(id+"F1.wireOp",EDGE,"E11.MirrorCS")])],"isStart":false});
            var Q52;
            {var subQ0=sQuery(id+"F1.wireOp",EDGE,"E0");Q52=makeQuery(id+"F2.opExtrude","CAP_EDGE",EDGE,{"disambiguationData":[OSD([subQ0]),TDD([makeQuery(id+"F1.imprint","IMPRINT",EDGE,{"disambiguationData":[TD([[makeQuery(id+"F1.imprint","INTERSECT",VERTEX,{"derivedFrom":[subQ0,sQuery(id+"F1.wireOp",EDGE,"E11.MirrorCS")]}),-1.0]])],"derivedFrom":subQ0})])],"isStart":false});}
            var Q53;
            Q53=makeQuery(id+"F2.opExtrude","CAP_EDGE",EDGE,{"disambiguationData":[OSD([sQuery(id+"F1.wireOp",EDGE,"E13.1.0")])],"isStart":false});
            var Q54;
            Q54=makeQuery(id+"F2.opExtrude","CAP_EDGE",EDGE,{"disambiguationData":[OSD([sQuery(id+"F1.wireOp",EDGE,"E13.1.2")])],"isStart":false});
            var Q55;
            {var subQ0=sQuery(id+"F1.wireOp",EDGE,"E0");Q55=makeQuery(id+"F2.opExtrude","CAP_EDGE",EDGE,{"disambiguationData":[OSD([subQ0]),TDD([makeQuery(id+"F1.imprint","IMPRINT",EDGE,{"disambiguationData":[TD([[makeQuery(id+"F1.imprint","INTERSECT",VERTEX,{"derivedFrom":[subQ0,sQuery(id+"F1.wireOp",EDGE,"E13.1.2")]}),-1.0]])],"derivedFrom":subQ0})])],"isStart":false});}
            var Q56;
            Q56=makeQuery(id+"F2.opExtrude","CAP_EDGE",EDGE,{"disambiguationData":[OSD([sQuery(id+"F1.wireOp",EDGE,"E13.2.0")])],"isStart":false});
            var Q57;
            Q57=makeQuery(id+"F2.opExtrude","CAP_EDGE",EDGE,{"disambiguationData":[OSD([sQuery(id+"F1.wireOp",EDGE,"E13.2.2")])],"isStart":false});
            var Q58;
            {var subQ0=sQuery(id+"F1.wireOp",EDGE,"E0");Q58=makeQuery(id+"F2.opExtrude","CAP_EDGE",EDGE,{"disambiguationData":[OSD([subQ0]),TDD([makeQuery(id+"F1.imprint","IMPRINT",EDGE,{"disambiguationData":[TD([[makeQuery(id+"F1.imprint","INTERSECT",VERTEX,{"derivedFrom":[subQ0,sQuery(id+"F1.wireOp",EDGE,"E13.2.2")]}),-1.0]])],"derivedFrom":subQ0})])],"isStart":false});}
            var Q59;
            Q59=makeQuery(id+"F2.opExtrude","CAP_EDGE",EDGE,{"disambiguationData":[OSD([sQuery(id+"F1.wireOp",EDGE,"E13.3.0")])],"isStart":false});
            var Q60;
            Q60=makeQuery(id+"F2.opExtrude","CAP_EDGE",EDGE,{"disambiguationData":[OSD([sQuery(id+"F1.wireOp",EDGE,"E13.3.2")])],"isStart":false});
            var Q61;
            {var subQ0=sQuery(id+"F1.wireOp",EDGE,"E0");Q61=makeQuery(id+"F2.opExtrude","CAP_EDGE",EDGE,{"disambiguationData":[OSD([subQ0]),TDD([makeQuery(id+"F1.imprint","IMPRINT",EDGE,{"disambiguationData":[TD([[makeQuery(id+"F1.imprint","INTERSECT",VERTEX,{"derivedFrom":[subQ0,sQuery(id+"F1.wireOp",EDGE,"E13.3.2")]}),-1.0]])],"derivedFrom":subQ0})])],"isStart":false});}
            var Q62;
            Q62=makeQuery(id+"F2.opExtrude","CAP_EDGE",EDGE,{"disambiguationData":[OSD([sQuery(id+"F1.wireOp",EDGE,"E13.4.0")])],"isStart":false});
            var Q63;
            Q63=makeQuery(id+"F2.opExtrude","CAP_EDGE",EDGE,{"disambiguationData":[OSD([sQuery(id+"F1.wireOp",EDGE,"E13.4.2")])],"isStart":false});
            var Q64;
            {var subQ0=sQuery(id+"F1.wireOp",EDGE,"E0");Q64=makeQuery(id+"F2.opExtrude","CAP_EDGE",EDGE,{"disambiguationData":[OSD([subQ0]),TDD([makeQuery(id+"F1.imprint","IMPRINT",EDGE,{"disambiguationData":[TD([[makeQuery(id+"F1.imprint","INTERSECT",VERTEX,{"derivedFrom":[subQ0,sQuery(id+"F1.wireOp",EDGE,"E13.4.2")]}),-1.0]])],"derivedFrom":subQ0})])],"isStart":false});}
            var Q65;
            {var subQ0=sQuery(id+"F1.wireOp",EDGE,"E0");Q65=makeQuery(id+"F2.opExtrude","CAP_EDGE",EDGE,{"disambiguationData":[OSD([subQ0]),TDD([makeQuery(id+"F1.imprint","IMPRINT",EDGE,{"disambiguationData":[TD([[makeQuery(id+"F1.imprint","INTERSECT",VERTEX,{"derivedFrom":[subQ0,sQuery(id+"F1.wireOp",EDGE,"E13.5.2")]}),-1.0]])],"derivedFrom":subQ0})])],"isStart":true});}
            var Q66;
            Q66=makeQuery(id+"F2.opExtrude","CAP_EDGE",EDGE,{"disambiguationData":[OSD([sQuery(id+"F1.wireOp",EDGE,"E13.5.2")])],"isStart":true});
            var Q67;
            {var subQ0=sQuery(id+"F1.wireOp",EDGE,"E0");Q67=makeQuery(id+"F2.opExtrude","CAP_EDGE",EDGE,{"disambiguationData":[OSD([subQ0]),TDD([makeQuery(id+"F1.imprint","IMPRINT",EDGE,{"disambiguationData":[TD([[makeQuery(id+"F1.imprint","INTERSECT",VERTEX,{"derivedFrom":[subQ0,sQuery(id+"F1.wireOp",EDGE,"E13.4.2")]}),-1.0]])],"derivedFrom":subQ0})])],"isStart":true});}
            var Q68;
            Q68=makeQuery(id+"F2.opExtrude","CAP_EDGE",EDGE,{"disambiguationData":[OSD([sQuery(id+"F1.wireOp",EDGE,"E13.4.2")])],"isStart":true});
            var Q69;
            Q69=makeQuery(id+"F2.opExtrude","CAP_EDGE",EDGE,{"disambiguationData":[OSD([sQuery(id+"F1.wireOp",EDGE,"E13.4.0")])],"isStart":true});
            var Q70;
            {var subQ0=sQuery(id+"F1.wireOp",EDGE,"E0");Q70=makeQuery(id+"F2.opExtrude","CAP_EDGE",EDGE,{"disambiguationData":[OSD([subQ0]),TDD([makeQuery(id+"F1.imprint","IMPRINT",EDGE,{"disambiguationData":[TD([[makeQuery(id+"F1.imprint","INTERSECT",VERTEX,{"derivedFrom":[subQ0,sQuery(id+"F1.wireOp",EDGE,"E13.3.2")]}),-1.0]])],"derivedFrom":subQ0})])],"isStart":true});}
            var Q71;
            Q71=makeQuery(id+"F2.opExtrude","CAP_EDGE",EDGE,{"disambiguationData":[OSD([sQuery(id+"F1.wireOp",EDGE,"E13.3.2")])],"isStart":true});
            var Q72;
            Q72=makeQuery(id+"F2.opExtrude","CAP_EDGE",EDGE,{"disambiguationData":[OSD([sQuery(id+"F1.wireOp",EDGE,"E13.3.0")])],"isStart":true});
            var Q73;
            {var subQ0=sQuery(id+"F1.wireOp",EDGE,"E0");Q73=makeQuery(id+"F2.opExtrude","CAP_EDGE",EDGE,{"disambiguationData":[OSD([subQ0]),TDD([makeQuery(id+"F1.imprint","IMPRINT",EDGE,{"disambiguationData":[TD([[makeQuery(id+"F1.imprint","INTERSECT",VERTEX,{"derivedFrom":[subQ0,sQuery(id+"F1.wireOp",EDGE,"E13.2.2")]}),-1.0]])],"derivedFrom":subQ0})])],"isStart":true});}
            var Q74;
            Q74=makeQuery(id+"F2.opExtrude","CAP_EDGE",EDGE,{"disambiguationData":[OSD([sQuery(id+"F1.wireOp",EDGE,"E13.2.2")])],"isStart":true});
            var Q75;
            Q75=makeQuery(id+"F2.opExtrude","CAP_EDGE",EDGE,{"disambiguationData":[OSD([sQuery(id+"F1.wireOp",EDGE,"E13.2.0")])],"isStart":true});
            var Q76;
            Q76=makeQuery(id+"F2.opExtrude","CAP_EDGE",EDGE,{"disambiguationData":[OSD([sQuery(id+"F1.wireOp",EDGE,"E13.1.2")])],"isStart":true});
            var Q77;
            {var subQ0=sQuery(id+"F1.wireOp",EDGE,"E0");Q77=makeQuery(id+"F2.opExtrude","CAP_EDGE",EDGE,{"disambiguationData":[OSD([subQ0]),TDD([makeQuery(id+"F1.imprint","IMPRINT",EDGE,{"disambiguationData":[TD([[makeQuery(id+"F1.imprint","INTERSECT",VERTEX,{"derivedFrom":[subQ0,sQuery(id+"F1.wireOp",EDGE,"E13.1.2")]}),-1.0]])],"derivedFrom":subQ0})])],"isStart":true});}
            var Q78;
            Q78=makeQuery(id+"F2.opExtrude","CAP_EDGE",EDGE,{"disambiguationData":[OSD([sQuery(id+"F1.wireOp",EDGE,"E13.1.0")])],"isStart":true});
            var Q79;
            {var subQ0=sQuery(id+"F1.wireOp",EDGE,"E0");Q79=makeQuery(id+"F2.opExtrude","CAP_EDGE",EDGE,{"disambiguationData":[OSD([subQ0]),TDD([makeQuery(id+"F1.imprint","IMPRINT",EDGE,{"disambiguationData":[TD([[makeQuery(id+"F1.imprint","INTERSECT",VERTEX,{"derivedFrom":[subQ0,sQuery(id+"F1.wireOp",EDGE,"E11.MirrorCS")]}),-1.0]])],"derivedFrom":subQ0})])],"isStart":true});}
            var Q80;
            Q80=makeQuery(id+"F2.opExtrude","CAP_EDGE",EDGE,{"disambiguationData":[OSD([sQuery(id+"F1.wireOp",EDGE,"E11.MirrorCS")])],"isStart":true});
            var Q81;
            Q81=makeQuery(id+"F2.opExtrude","CAP_EDGE",EDGE,{"disambiguationData":[OSD([sQuery(id+"F1.wireOp",EDGE,"E10.trimOffspring")])],"isStart":true});
            var Q82;
            {var subQ0=sQuery(id+"F1.wireOp",EDGE,"E0");Q82=makeQuery(id+"F2.opExtrude","CAP_EDGE",EDGE,{"disambiguationData":[OSD([subQ0]),TDD([makeQuery(id+"F1.imprint","IMPRINT",EDGE,{"disambiguationData":[TD([[makeQuery(id+"F1.imprint","INTERSECT",VERTEX,{"derivedFrom":[subQ0,sQuery(id+"F1.wireOp",EDGE,"E10.trimOffspring")]}),1.0]])],"derivedFrom":subQ0})])],"isStart":true});}
            var Q83;
            Q83=makeQuery(id+"F2.opExtrude","CAP_EDGE",EDGE,{"disambiguationData":[OSD([sQuery(id+"F1.wireOp",EDGE,"E13.19.2")])],"isStart":true});
            var Q84;
            Q84=makeQuery(id+"F2.opExtrude","CAP_EDGE",EDGE,{"disambiguationData":[OSD([sQuery(id+"F1.wireOp",EDGE,"E13.19.0")])],"isStart":true});
            var Q85;
            {var subQ0=sQuery(id+"F1.wireOp",EDGE,"E0");Q85=makeQuery(id+"F2.opExtrude","CAP_EDGE",EDGE,{"disambiguationData":[OSD([subQ0]),TDD([makeQuery(id+"F1.imprint","IMPRINT",EDGE,{"disambiguationData":[TD([[makeQuery(id+"F1.imprint","INTERSECT",VERTEX,{"derivedFrom":[subQ0,sQuery(id+"F1.wireOp",EDGE,"E13.18.2")]}),-1.0]])],"derivedFrom":subQ0})])],"isStart":true});}
            var Q86;
            Q86=makeQuery(id+"F2.opExtrude","CAP_EDGE",EDGE,{"disambiguationData":[OSD([sQuery(id+"F1.wireOp",EDGE,"E13.18.2")])],"isStart":true});
            var Q87;
            Q87=makeQuery(id+"F2.opExtrude","CAP_EDGE",EDGE,{"disambiguationData":[OSD([sQuery(id+"F1.wireOp",EDGE,"E13.18.0")])],"isStart":true});
            var Q88;
            {var subQ0=sQuery(id+"F1.wireOp",EDGE,"E0");Q88=makeQuery(id+"F2.opExtrude","CAP_EDGE",EDGE,{"disambiguationData":[OSD([subQ0]),TDD([makeQuery(id+"F1.imprint","IMPRINT",EDGE,{"disambiguationData":[TD([[makeQuery(id+"F1.imprint","INTERSECT",VERTEX,{"derivedFrom":[subQ0,sQuery(id+"F1.wireOp",EDGE,"E13.17.2")]}),-1.0]])],"derivedFrom":subQ0})])],"isStart":true});}
            var Q89;
            Q89=makeQuery(id+"F2.opExtrude","CAP_EDGE",EDGE,{"disambiguationData":[OSD([sQuery(id+"F1.wireOp",EDGE,"E13.17.2")])],"isStart":true});
            var Q90;
            Q90=makeQuery(id+"F2.opExtrude","CAP_EDGE",EDGE,{"disambiguationData":[OSD([sQuery(id+"F1.wireOp",EDGE,"E13.17.0")])],"isStart":true});
            var Q91;
            {var subQ0=sQuery(id+"F1.wireOp",EDGE,"E0");Q91=makeQuery(id+"F2.opExtrude","CAP_EDGE",EDGE,{"disambiguationData":[OSD([subQ0]),TDD([makeQuery(id+"F1.imprint","IMPRINT",EDGE,{"disambiguationData":[TD([[makeQuery(id+"F1.imprint","INTERSECT",VERTEX,{"derivedFrom":[subQ0,sQuery(id+"F1.wireOp",EDGE,"E13.16.2")]}),-1.0]])],"derivedFrom":subQ0})])],"isStart":true});}
            var Q92;
            Q92=makeQuery(id+"F2.opExtrude","CAP_EDGE",EDGE,{"disambiguationData":[OSD([sQuery(id+"F1.wireOp",EDGE,"E13.16.2")])],"isStart":true});
            var Q93;
            Q93=makeQuery(id+"F2.opExtrude","CAP_EDGE",EDGE,{"disambiguationData":[OSD([sQuery(id+"F1.wireOp",EDGE,"E13.16.0")])],"isStart":true});
            var Q94;
            {var subQ0=sQuery(id+"F1.wireOp",EDGE,"E0");Q94=makeQuery(id+"F2.opExtrude","CAP_EDGE",EDGE,{"disambiguationData":[OSD([subQ0]),TDD([makeQuery(id+"F1.imprint","IMPRINT",EDGE,{"disambiguationData":[TD([[makeQuery(id+"F1.imprint","INTERSECT",VERTEX,{"derivedFrom":[subQ0,sQuery(id+"F1.wireOp",EDGE,"E13.15.2")]}),-1.0]])],"derivedFrom":subQ0})])],"isStart":true});}
            var Q95;
            Q95=makeQuery(id+"F2.opExtrude","CAP_EDGE",EDGE,{"disambiguationData":[OSD([sQuery(id+"F1.wireOp",EDGE,"E13.15.2")])],"isStart":true});
            var Q96;
            Q96=makeQuery(id+"F2.opExtrude","CAP_EDGE",EDGE,{"disambiguationData":[OSD([sQuery(id+"F1.wireOp",EDGE,"E13.15.0")])],"isStart":true});
            var Q97;
            {var subQ0=sQuery(id+"F1.wireOp",EDGE,"E0");Q97=makeQuery(id+"F2.opExtrude","CAP_EDGE",EDGE,{"disambiguationData":[OSD([subQ0]),TDD([makeQuery(id+"F1.imprint","IMPRINT",EDGE,{"disambiguationData":[TD([[makeQuery(id+"F1.imprint","INTERSECT",VERTEX,{"derivedFrom":[subQ0,sQuery(id+"F1.wireOp",EDGE,"E13.14.2")]}),-1.0]])],"derivedFrom":subQ0})])],"isStart":true});}
            var Q98;
            Q98=makeQuery(id+"F2.opExtrude","CAP_EDGE",EDGE,{"disambiguationData":[OSD([sQuery(id+"F1.wireOp",EDGE,"E13.14.2")])],"isStart":true});
            var Q99;
            Q99=makeQuery(id+"F2.opExtrude","CAP_EDGE",EDGE,{"disambiguationData":[OSD([sQuery(id+"F1.wireOp",EDGE,"E13.14.0")])],"isStart":true});
            var Q100;
            {var subQ0=sQuery(id+"F1.wireOp",EDGE,"E0");Q100=makeQuery(id+"F2.opExtrude","CAP_EDGE",EDGE,{"disambiguationData":[OSD([subQ0]),TDD([makeQuery(id+"F1.imprint","IMPRINT",EDGE,{"disambiguationData":[TD([[makeQuery(id+"F1.imprint","INTERSECT",VERTEX,{"derivedFrom":[subQ0,sQuery(id+"F1.wireOp",EDGE,"E13.13.2")]}),-1.0]])],"derivedFrom":subQ0})])],"isStart":true});}
            var Q101;
            Q101=makeQuery(id+"F2.opExtrude","CAP_EDGE",EDGE,{"disambiguationData":[OSD([sQuery(id+"F1.wireOp",EDGE,"E13.13.2")])],"isStart":true});
            var Q102;
            Q102=makeQuery(id+"F2.opExtrude","CAP_EDGE",EDGE,{"disambiguationData":[OSD([sQuery(id+"F1.wireOp",EDGE,"E13.13.0")])],"isStart":true});
            var Q103;
            {var subQ0=sQuery(id+"F1.wireOp",EDGE,"E0");Q103=makeQuery(id+"F2.opExtrude","CAP_EDGE",EDGE,{"disambiguationData":[OSD([subQ0]),TDD([makeQuery(id+"F1.imprint","IMPRINT",EDGE,{"disambiguationData":[TD([[makeQuery(id+"F1.imprint","INTERSECT",VERTEX,{"derivedFrom":[subQ0,sQuery(id+"F1.wireOp",EDGE,"E13.12.2")]}),-1.0]])],"derivedFrom":subQ0})])],"isStart":true});}
            var Q104;
            Q104=makeQuery(id+"F2.opExtrude","CAP_EDGE",EDGE,{"disambiguationData":[OSD([sQuery(id+"F1.wireOp",EDGE,"E13.12.2")])],"isStart":true});
            var Q105;
            Q105=makeQuery(id+"F2.opExtrude","CAP_EDGE",EDGE,{"disambiguationData":[OSD([sQuery(id+"F1.wireOp",EDGE,"E13.12.0")])],"isStart":true});
            var Q106;
            {var subQ0=sQuery(id+"F1.wireOp",EDGE,"E0");Q106=makeQuery(id+"F2.opExtrude","CAP_EDGE",EDGE,{"disambiguationData":[OSD([subQ0]),TDD([makeQuery(id+"F1.imprint","IMPRINT",EDGE,{"disambiguationData":[TD([[makeQuery(id+"F1.imprint","INTERSECT",VERTEX,{"derivedFrom":[subQ0,sQuery(id+"F1.wireOp",EDGE,"E13.11.2")]}),-1.0]])],"derivedFrom":subQ0})])],"isStart":true});}
            var Q107;
            Q107=makeQuery(id+"F2.opExtrude","CAP_EDGE",EDGE,{"disambiguationData":[OSD([sQuery(id+"F1.wireOp",EDGE,"E13.11.2")])],"isStart":true});
            var Q108;
            Q108=makeQuery(id+"F2.opExtrude","CAP_EDGE",EDGE,{"disambiguationData":[OSD([sQuery(id+"F1.wireOp",EDGE,"E13.11.0")])],"isStart":true});
            var Q109;
            {var subQ0=sQuery(id+"F1.wireOp",EDGE,"E0");Q109=makeQuery(id+"F2.opExtrude","CAP_EDGE",EDGE,{"disambiguationData":[OSD([subQ0]),TDD([makeQuery(id+"F1.imprint","IMPRINT",EDGE,{"disambiguationData":[TD([[makeQuery(id+"F1.imprint","INTERSECT",VERTEX,{"derivedFrom":[subQ0,sQuery(id+"F1.wireOp",EDGE,"E13.10.2")]}),-1.0]])],"derivedFrom":subQ0})])],"isStart":true});}
            var Q110;
            Q110=makeQuery(id+"F2.opExtrude","CAP_EDGE",EDGE,{"disambiguationData":[OSD([sQuery(id+"F1.wireOp",EDGE,"E13.10.2")])],"isStart":true});
            var Q111;
            Q111=makeQuery(id+"F2.opExtrude","CAP_EDGE",EDGE,{"disambiguationData":[OSD([sQuery(id+"F1.wireOp",EDGE,"E13.10.0")])],"isStart":true});
            var Q112;
            {var subQ0=sQuery(id+"F1.wireOp",EDGE,"E0");Q112=makeQuery(id+"F2.opExtrude","CAP_EDGE",EDGE,{"disambiguationData":[OSD([subQ0]),TDD([makeQuery(id+"F1.imprint","IMPRINT",EDGE,{"disambiguationData":[TD([[makeQuery(id+"F1.imprint","INTERSECT",VERTEX,{"derivedFrom":[subQ0,sQuery(id+"F1.wireOp",EDGE,"E13.9.2")]}),-1.0]])],"derivedFrom":subQ0})])],"isStart":true});}
            var Q113;
            Q113=makeQuery(id+"F2.opExtrude","CAP_EDGE",EDGE,{"disambiguationData":[OSD([sQuery(id+"F1.wireOp",EDGE,"E13.9.2")])],"isStart":true});
            var Q114;
            Q114=makeQuery(id+"F2.opExtrude","CAP_EDGE",EDGE,{"disambiguationData":[OSD([sQuery(id+"F1.wireOp",EDGE,"E13.9.0")])],"isStart":true});
            var Q115;
            {var subQ0=sQuery(id+"F1.wireOp",EDGE,"E0");Q115=makeQuery(id+"F2.opExtrude","CAP_EDGE",EDGE,{"disambiguationData":[OSD([subQ0]),TDD([makeQuery(id+"F1.imprint","IMPRINT",EDGE,{"disambiguationData":[TD([[makeQuery(id+"F1.imprint","INTERSECT",VERTEX,{"derivedFrom":[subQ0,sQuery(id+"F1.wireOp",EDGE,"E13.8.2")]}),-1.0]])],"derivedFrom":subQ0})])],"isStart":true});}
            var Q116;
            Q116=makeQuery(id+"F2.opExtrude","CAP_EDGE",EDGE,{"disambiguationData":[OSD([sQuery(id+"F1.wireOp",EDGE,"E13.8.2")])],"isStart":true});
            fillet(context, id + "F3", {"entities" : qUnion([Q0, Q1, Q2, Q3, Q4, Q5, Q6, Q7, Q8, Q9, Q10, Q11, Q12, Q13, Q14, Q15, Q16, Q17, Q18, Q19, Q20, Q21, Q22, Q23, Q24, Q25, Q26, Q27, Q28, Q29, Q30, Q31, Q32, Q33, Q34, Q35, Q36, Q37, Q38, Q39, Q40, Q41, Q42, Q43, Q44, Q45, Q46, Q47, Q48, Q49, Q50, Q51, Q52, Q53, Q54, Q55, Q56, Q57, Q58, Q59, Q60, Q61, Q62, Q63, Q64, Q65, Q66, Q67, Q68, Q69, Q70, Q71, Q72, Q73, Q74, Q75, Q76, Q77, Q78, Q79, Q80, Q81, Q82, Q83, Q84, Q85, Q86, Q87, Q88, Q89, Q90, Q91, Q92, Q93, Q94, Q95, Q96, Q97, Q98, Q99, Q100, Q101, Q102, Q103, Q104, Q105, Q106, Q107, Q108, Q109, Q110, Q111, Q112, Q113, Q114, Q115, Q116]), "radius" : .15 * mm, "tangentPropagation" : true, "allowEdgeOverflow" : false});
        }
    });
